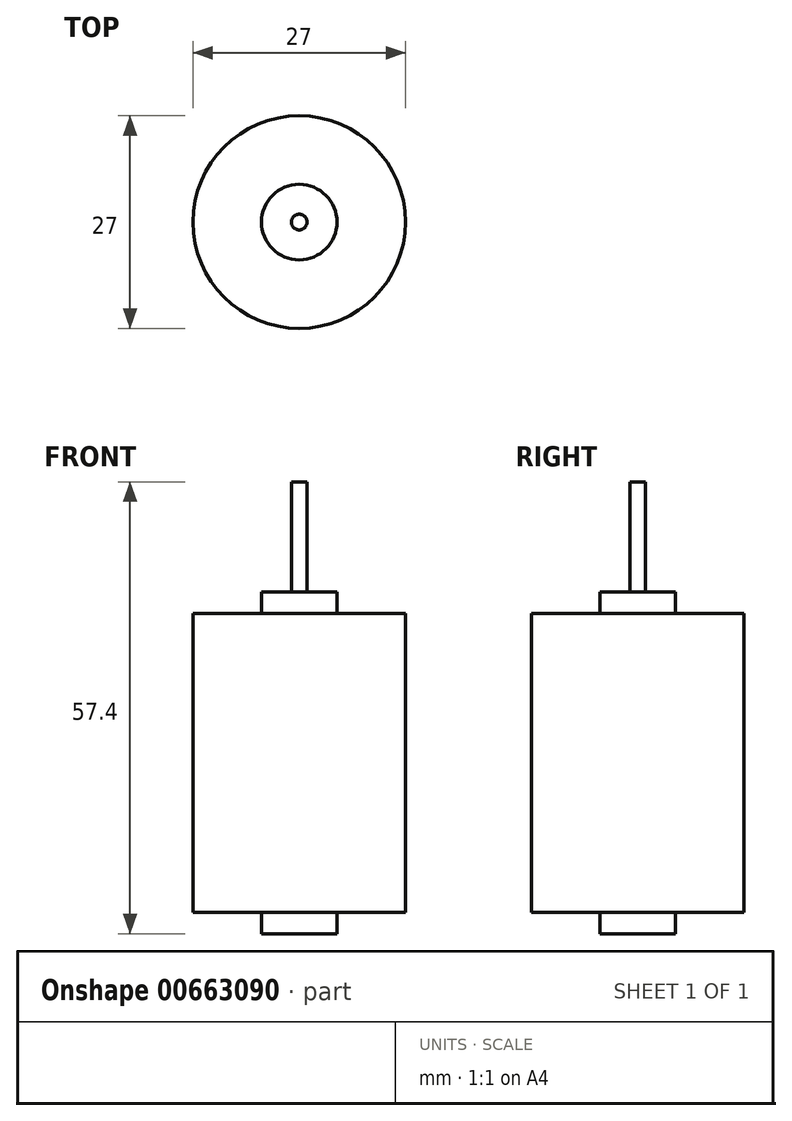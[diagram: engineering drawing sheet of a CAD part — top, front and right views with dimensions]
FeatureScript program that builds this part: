
annotation { "Feature Type Name" : "Feature", "Feature Type Description" : "" }
export const myFeature = defineFeature(function(context is Context, id is Id, definition is map)
    precondition{}
    {
        {
            var Q0;
            Q0=qCreatedBy(makeId("Right.planeOp"),FACE);
            var sketch = newSketch(context, id + "F0", { "sketchPlane" : qUnion([Q0])});
            skLineSegment(sketch, "E0", {"start": v(0, 0) * mm, "end": v(4.8, 0) * mm});
            skLineSegment(sketch, "E1", {"start": v(4.8, 0) * mm, "end": v(4.8, 2.7) * mm});
            skLineSegment(sketch, "E2", {"start": v(4.8, 2.7) * mm, "end": v(13.5, 2.7) * mm});
            skLineSegment(sketch, "E3", {"start": v(13.5, 2.7) * mm, "end": v(13.5, 40.7) * mm});
            skLineSegment(sketch, "E4", {"start": v(13.5, 40.7) * mm, "end": v(4.8, 40.7) * mm});
            skLineSegment(sketch, "E5", {"start": v(4.8, 40.7) * mm, "end": v(4.8, 43.4) * mm});
            skLineSegment(sketch, "E6", {"start": v(4.8, 43.4) * mm, "end": v(1, 43.4) * mm});
            skLineSegment(sketch, "E7", {"start": v(1, 43.4) * mm, "end": v(1, 57.4) * mm});
            skLineSegment(sketch, "E8", {"start": v(1, 57.4) * mm, "end": v(0, 57.4) * mm});
            skLineSegment(sketch, "E9", {"start": v(0, 57.4) * mm, "end": v(0, 0) * mm});
            skSolve(sketch);
        }
        {
            var Q0;
            Q0=makeQuery(id+"F0.imprint","IMPRINT",FACE,{"disambiguationData":[TD([[makeQuery(id+"F0.imprint","IMPRINT",EDGE,{"derivedFrom":sQuery(id+"F0.wireOp",EDGE,"E0")}),1.0]])]});
            var Q1;
            Q1=sQuery(id+"F0.wireOp",EDGE,"E9");
            revolve(context, id + "F1", {"surfaceOperationType" : NewSurfaceOperationType.NEW, "entities" : qUnion([Q0]), "axis" : qUnion([Q1]), "revolveType" : RevolveType.FULL});
        }
    });
